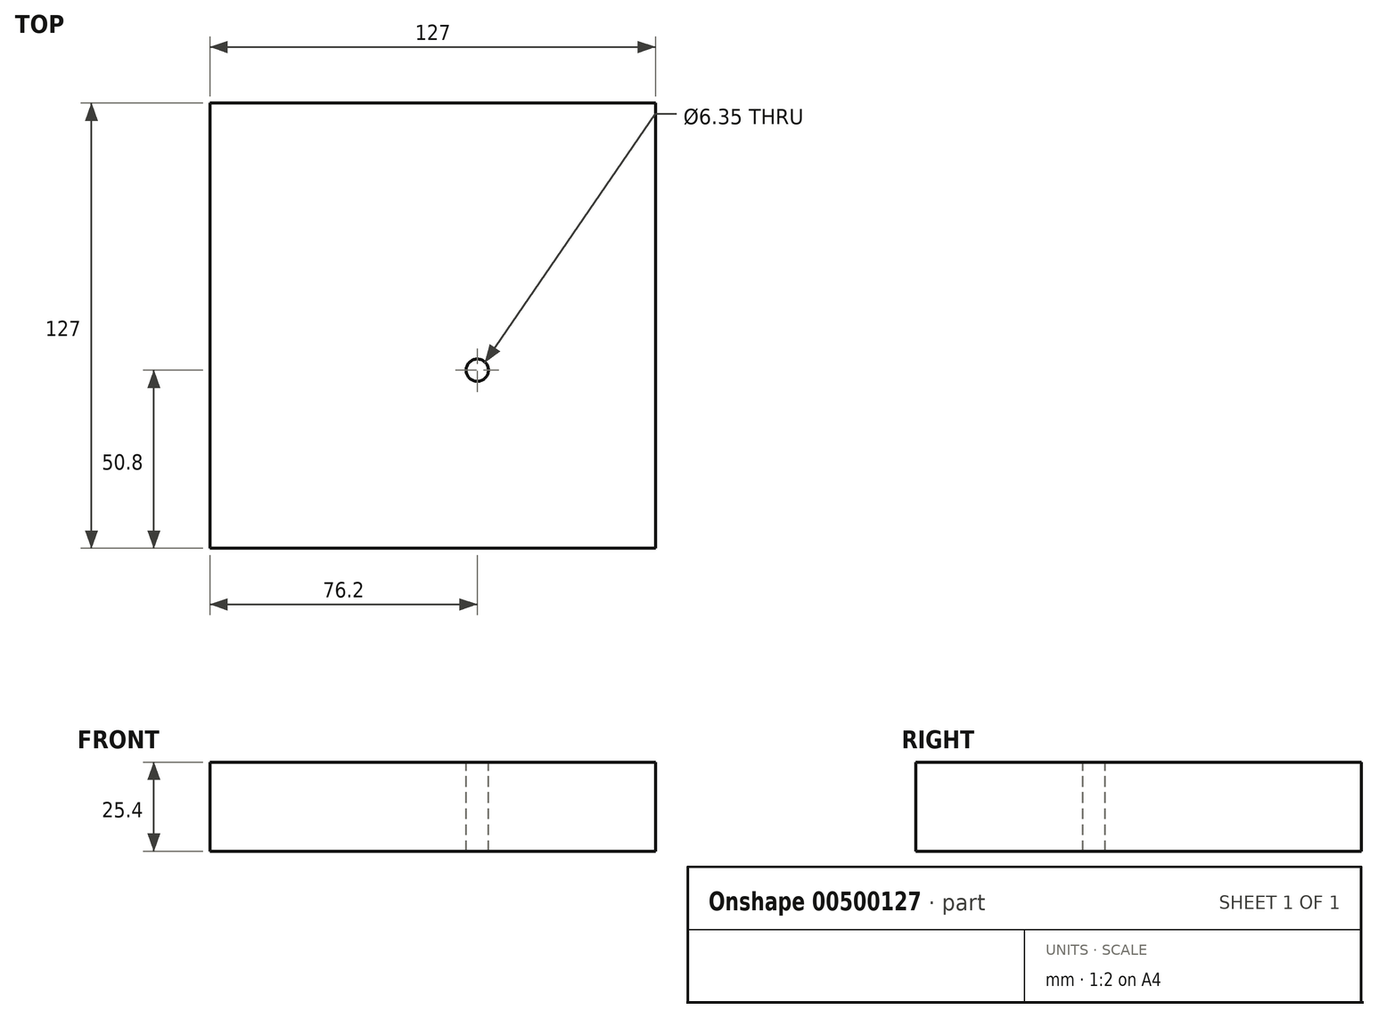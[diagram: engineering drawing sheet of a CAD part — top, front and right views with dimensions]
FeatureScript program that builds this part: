
annotation { "Feature Type Name" : "Feature", "Feature Type Description" : "" }
export const myFeature = defineFeature(function(context is Context, id is Id, definition is map)
    precondition{}
    {
        {
            var Q0;
            Q0=qCreatedBy(makeId("Top.planeOp"),FACE);
            var sketch = newSketch(context, id + "F0", { "sketchPlane" : qUnion([Q0])});
            skLineSegment(sketch, "E0.bottom", {"start": v(0, 0) * mm, "end": v(-127, 0) * mm});
            skLineSegment(sketch, "E0.top", {"start": v(0, 127) * mm, "end": v(-127, 127) * mm});
            skLineSegment(sketch, "E0.left", {"start": v(0, 0) * mm, "end": v(0, 127) * mm});
            skLineSegment(sketch, "E0.right", {"start": v(-127, 0) * mm, "end": v(-127, 127) * mm});
            skSolve(sketch);
        }
        {
            var Q0;
            Q0 = qSketchRegion(id + "F0", true);
            extrude(context, id + "F1", {"entities" : qUnion([Q0]), "depth" : 25.4 * mm});
        }
        {
            var Q0;
            Q0=makeQuery(id+"F1.opExtrude","CAP_FACE",FACE,{"disambiguationData":[OSD([sQuery(id+"F0.wireOp",EDGE,"E0.bottom"),sQuery(id+"F0.wireOp",EDGE,"E0.top"),sQuery(id+"F0.wireOp",EDGE,"E0.left"),sQuery(id+"F0.wireOp",EDGE,"E0.right")])],"isStart":false});
            var sketch = newSketch(context, id + "F2", { "sketchPlane" : qUnion([Q0])});
            skLineSegment(sketch, "E1", {"start": v(0, 0) * mm, "end": v(0, 50.8) * mm});
            skLineSegment(sketch, "E2", {"start": v(0, 50.8) * mm, "end": v(-50.8, 50.8) * mm});
            skSolve(sketch);
        }
        {
            var Q0;
            Q0=sQuery(id+"F2.wireOp",VERTEX,"E2.end");
            var Q1;
            Q1=makeQuery(id+"F1.opExtrude","SWEPT_BODY",BODY,{"disambiguationData":[OSD([sQuery(id+"F0.wireOp",EDGE,"E0.bottom"),sQuery(id+"F0.wireOp",EDGE,"E0.top"),sQuery(id+"F0.wireOp",EDGE,"E0.left"),sQuery(id+"F0.wireOp",EDGE,"E0.right")])]});
            hole(context, id + "F3", {"style" : HoleStyle.SIMPLE, "endStyle" : HoleEndStyle.THROUGH, "holeDiameter" : 6.35 * mm, "isTappedThrough" : true, "tappedDepth" : 12.7 * mm, "tapClearance" : 3, "locations" : qUnion([Q0]), "scope" : qUnion([Q1])});
        }
    });
